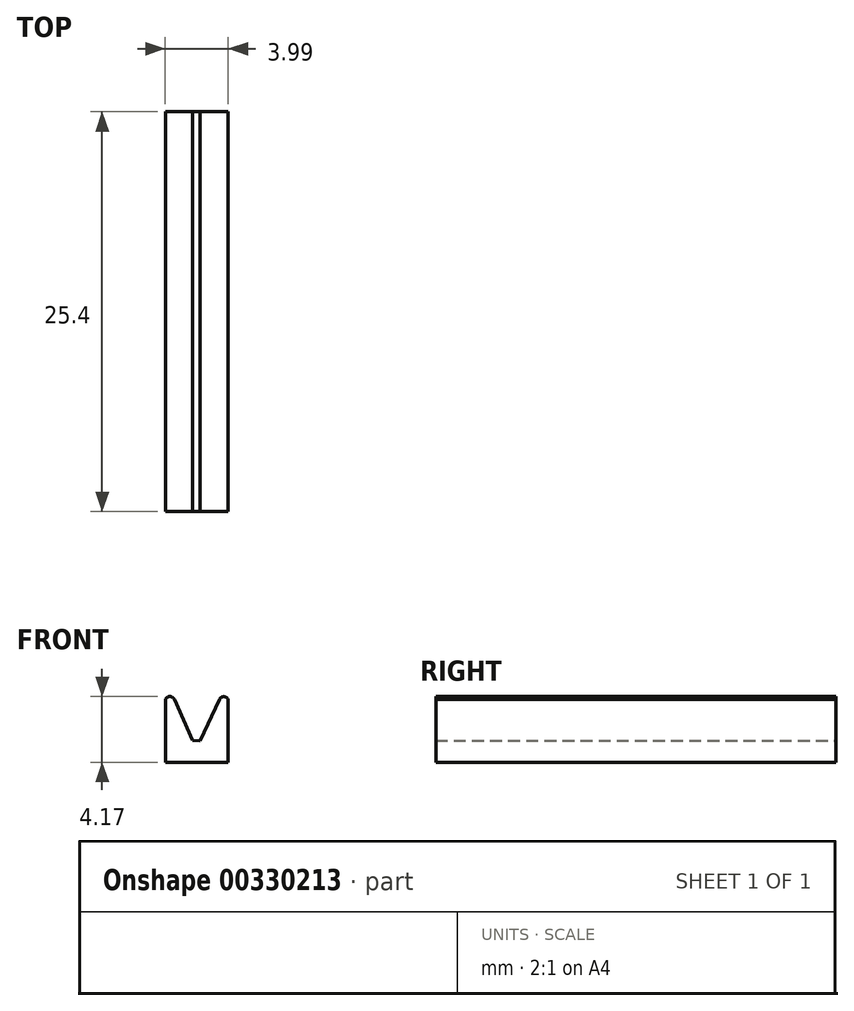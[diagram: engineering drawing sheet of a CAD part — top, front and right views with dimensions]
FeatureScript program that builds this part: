
annotation { "Feature Type Name" : "Feature", "Feature Type Description" : "" }
export const myFeature = defineFeature(function(context is Context, id is Id, definition is map)
    precondition{}
    {
        {
            var Q0;
            Q0=qCreatedBy(makeId("Front.planeOp"),FACE);
            var sketch = newSketch(context, id + "F0", { "sketchPlane" : qUnion([Q0])});
            skLineSegment(sketch, "E0.bottom", {"start": v(2.06, -1) * mm, "end": v(-1.93, -1) * mm});
            skLineSegment(sketch, "E0.left", {"start": v(2.06, -1) * mm, "end": v(2.06, 3) * mm});
            skLineSegment(sketch, "E0.right", {"start": v(-1.93, -1) * mm, "end": v(-1.93, 3) * mm});
            skLineSegment(sketch, "E1", {"start": v(-1.36, 3) * mm, "end": v(-0.2, 0.4) * mm});
            skLineSegment(sketch, "E2", {"start": v(1.5, 3) * mm, "end": v(0.3, 0.38) * mm});
            skArc(sketch, "E3", {"start": v(-1.36, 3) * mm, "mid": v(-1.64, 3.18) * mm, "end": v(-1.93, 3) * mm});
            skArc(sketch, "E4", {"start": v(1.5, 3) * mm, "mid": v(1.78, 3.18) * mm, "end": v(2.06, 3) * mm});
            skLineSegment(sketch, "E5", {"start": v(2.06, 3) * mm, "end": v(2.06, 4.86) * mm});
            skLineSegment(sketch, "E6", {"start": v(2.06, 4.86) * mm, "end": v(0.58, 4.86) * mm});
            skLineSegment(sketch, "E7", {"start": v(0.58, 4.86) * mm, "end": v(0.58, 4.37) * mm});
            skLineSegment(sketch, "E8", {"start": v(0.58, 4.37) * mm, "end": v(1.5, 4.37) * mm});
            skLineSegment(sketch, "E9", {"start": v(1.5, 4.37) * mm, "end": v(1.5, 3) * mm});
            skLineSegment(sketch, "E10", {"start": v(-0.2, 0.4) * mm, "end": v(0.3, 0.38) * mm});
            skSolve(sketch);
        }
        {
            var Q0;
            {var subQ3=sQuery(id+"F0.wireOp",EDGE,"ylV9YZef-2tfM-5KXM-l7S7-7uPfobgMoASA");Q0=makeQuery(id+"F0.imprint","IMPRINT",FACE,{"disambiguationData":[TD([[makeQuery(id+"F0.imprint","IMPRINT",EDGE,{"derivedFrom":subQ3}),1.0]])]});}
            var Q1;
            Q1=makeQuery(id+"F0.imprint","IMPRINT",FACE,{"disambiguationData":[TD([[makeQuery(id+"F0.imprint","IMPRINT",EDGE,{"derivedFrom":sQuery(id+"F0.wireOp",EDGE,"E0.bottom")}),-1.0]])]});
            var Q2;
            Q2=makeQuery(id+"F0.imprint","IMPRINT",FACE,{"disambiguationData":[TD([[makeQuery(id+"F0.imprint","IMPRINT",EDGE,{"derivedFrom":sQuery(id+"F0.wireOp",EDGE,"E4")}),1.0]])]});
            extrude(context, id + "F1", {"entities" : qUnion([Q0, Q1, Q2]), "depth" : 25.4 * mm});
        }
    });
